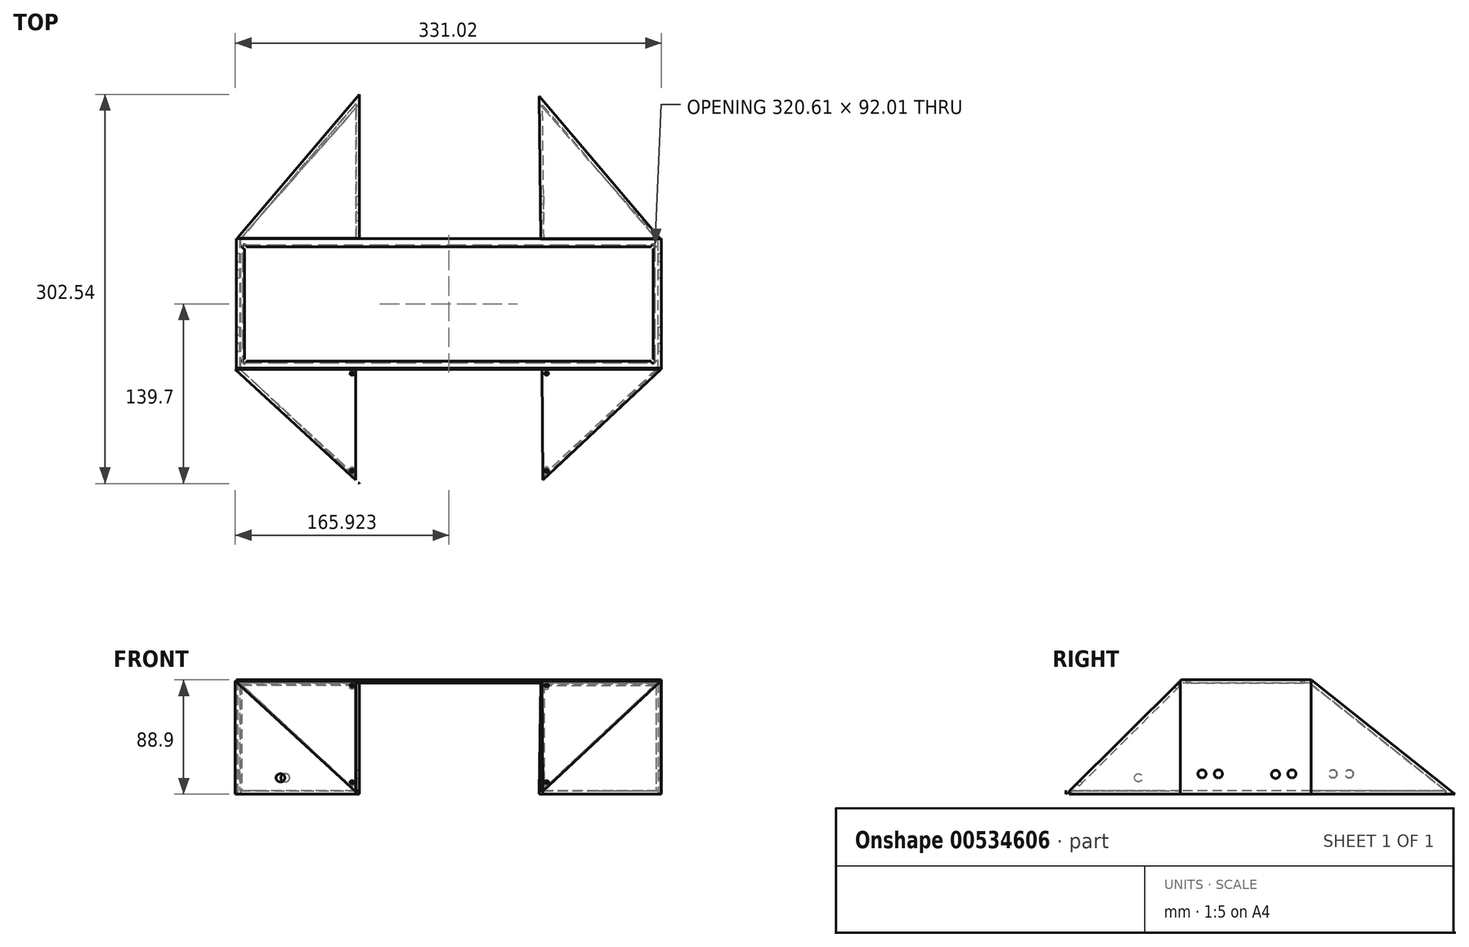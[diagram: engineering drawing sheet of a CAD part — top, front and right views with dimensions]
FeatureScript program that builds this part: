
annotation { "Feature Type Name" : "Feature", "Feature Type Description" : "" }
export const myFeature = defineFeature(function(context is Context, id is Id, definition is map)
    precondition{}
    {
        {
            var Q0;
            Q0=qCreatedBy(makeId("Right.planeOp"),FACE);
            var sketch = newSketch(context, id + "F0", { "sketchPlane" : qUnion([Q0])});
            skLineSegment(sketch, "E0", {"start": v(0, 0) * mm, "end": v(-88.9, 0) * mm});
            skLineSegment(sketch, "E1", {"start": v(-88.9, 0) * mm, "end": v(0, 88.9) * mm});
            skLineSegment(sketch, "E2", {"start": v(101.6, 0) * mm, "end": v(215.9, 0) * mm});
            skLineSegment(sketch, "E3", {"start": v(101.6, 0) * mm, "end": v(101.6, 88.9) * mm});
            skLineSegment(sketch, "E4", {"start": v(0, 88.9) * mm, "end": v(0, 0) * mm});
            skLineSegment(sketch, "E5", {"start": v(101.6, 88.9) * mm, "end": v(215.9, 0) * mm});
            skSolve(sketch);
        }
        {
            var Q0;
            Q0=qCreatedBy(makeId("Top.planeOp"),FACE);
            var sketch = newSketch(context, id + "F1", { "sketchPlane" : qUnion([Q0])});
            skLineSegment(sketch, "E6", {"start": v(-95.65, 101.6) * mm, "end": v(-95.65, 0) * mm});
            skLineSegment(sketch, "E7", {"start": v(234.55, 0) * mm, "end": v(234.55, 101.6) * mm});
            skLineSegment(sketch, "E8", {"start": v(-95.65, 0) * mm, "end": v(234.55, 0) * mm});
            skLineSegment(sketch, "E9", {"start": v(234.55, 101.6) * mm, "end": v(-95.65, 101.6) * mm});
            skSolve(sketch);
        }
        {
            var Q0;
            Q0=makeQuery(id+"F1.imprint","IMPRINT",FACE,{"disambiguationData":[TD([[makeQuery(id+"F1.imprint","IMPRINT",EDGE,{"derivedFrom":sQuery(id+"F1.wireOp",EDGE,"E6")}),1.0]])]});
            extrude(context, id + "F2", {"entities" : qUnion([Q0]), "depth" : 88.9 * mm, "offsetDistance" : 25.4 * mm});
        }
        {
            var Q0;
            Q0=makeQuery(id+"F2.opExtrude","SWEPT_FACE",FACE,{"disambiguationData":[OSD([sQuery(id+"F1.wireOp",EDGE,"E8")])]});
            var Q1;
            Q1=makeQuery(id+"F2.opExtrude","SWEPT_FACE",FACE,{"disambiguationData":[OSD([sQuery(id+"F1.wireOp",EDGE,"E9")])]});
            shell(context, id + "F3", {"entities" : qUnion([Q0, Q1]), "thickness" : 2.54 * mm});
        }
        {
            var Q0;
            Q0=qCreatedBy(makeId("Top.planeOp"),FACE);
            var sketch = newSketch(context, id + "F4", { "sketchPlane" : qUnion([Q0])});
            skLineSegment(sketch, "E10", {"start": v(0, 213.64) * mm, "end": v(-94.8, 102.22) * mm});
            skLineSegment(sketch, "E11", {"start": v(0, 213.64) * mm, "end": v(0, 101.72) * mm});
            skLineSegment(sketch, "E12", {"start": v(0, 101.72) * mm, "end": v(-94.8, 102.22) * mm});
            skLineSegment(sketch, "E13", {"start": v(139.7, 212.38) * mm, "end": v(233.9, 101.28) * mm});
            skLineSegment(sketch, "E14", {"start": v(233.9, 101.28) * mm, "end": v(140.82, 101.28) * mm});
            skLineSegment(sketch, "E15", {"start": v(140.82, 101.28) * mm, "end": v(139.7, 212.38) * mm});
            skLineSegment(sketch, "E16", {"start": v(0, -88.9) * mm, "end": v(-96.47, 0) * mm});
            skLineSegment(sketch, "E17", {"start": v(-96.47, 0) * mm, "end": v(0, 0) * mm});
            skLineSegment(sketch, "E18", {"start": v(0, 0) * mm, "end": v(0, -88.9) * mm});
            skLineSegment(sketch, "E19", {"start": v(234.3, 0) * mm, "end": v(139.7, -88.9) * mm});
            skLineSegment(sketch, "E20", {"start": v(139.7, -88.9) * mm, "end": v(138.93, 0) * mm});
            skLineSegment(sketch, "E21", {"start": v(138.93, 0) * mm, "end": v(234.3, 0) * mm});
            skSolve(sketch);
        }
        {
            var Q0;
            Q0 = qSketchRegion(id + "F4", true);
            extrude(context, id + "F5", {"entities" : qUnion([Q0]), "depth" : 88.9 * mm, "offsetDistance" : 25.4 * mm});
        }
        {
            var Q0;
            Q0=qCreatedBy(makeId("Right.planeOp"),FACE);
            var sketch = newSketch(context, id + "F6", { "sketchPlane" : qUnion([Q0])});
            skLineSegment(sketch, "E22", {"start": v(55.29, 143) * mm, "end": v(-109.68, 111.35) * mm});
            skLineSegment(sketch, "E23", {"start": v(-109.68, 111.35) * mm, "end": v(-88.32, 0) * mm});
            skLineSegment(sketch, "E24", {"start": v(-88.32, 0) * mm, "end": v(55.29, 143) * mm});
            skLineSegment(sketch, "E25", {"start": v(101.57, 88.88) * mm, "end": v(213.71, 0) * mm});
            skLineSegment(sketch, "E26", {"start": v(101.57, 88.88) * mm, "end": v(221.04, 116.12) * mm});
            skLineSegment(sketch, "E27", {"start": v(221.04, 116.12) * mm, "end": v(213.71, 0) * mm});
            skSolve(sketch);
        }
        {
            var Q0;
            Q0 = qSketchRegion(id + "F6", true);
            extrude(context, id + "F7", {"entities" : qUnion([Q0]), "operationType" : NewBodyOperationType.REMOVE, "oppositeDirection" : true, "depth" : 254 * mm, "offsetDistance" : 25.4 * mm});
        }
        {
            var Q0;
            Q0 = qSketchRegion(id + "F6", true);
            extrude(context, id + "F8", {"entities" : qUnion([Q0]), "operationType" : NewBodyOperationType.REMOVE, "depth" : 381 * mm, "offsetDistance" : 25.4 * mm});
        }
        {
            var Q0;
            Q0=qCreatedBy(makeId("Top.planeOp"),FACE);
            var sketch = newSketch(context, id + "F9", { "sketchPlane" : qUnion([Q0])});
            skLineSegment(sketch, "E28.bottom", {"start": v(-89.3, 95.25) * mm, "end": v(228.2, 95.25) * mm});
            skLineSegment(sketch, "E28.top", {"start": v(-89.3, 6.35) * mm, "end": v(228.2, 6.35) * mm});
            skLineSegment(sketch, "E28.left", {"start": v(-89.3, 95.25) * mm, "end": v(-89.3, 6.35) * mm});
            skLineSegment(sketch, "E28.right", {"start": v(228.2, 95.25) * mm, "end": v(228.2, 6.35) * mm});
            skSolve(sketch);
        }
        {
            var Q0;
            Q0 = qSketchRegion(id + "F9", true);
            var Q1;
            Q1=makeQuery(id+"F2.opExtrude","CAP_FACE",FACE,{"disambiguationData":[OSD([sQuery(id+"F1.wireOp",EDGE,"E6"),sQuery(id+"F1.wireOp",EDGE,"E7"),sQuery(id+"F1.wireOp",EDGE,"E8"),sQuery(id+"F1.wireOp",EDGE,"E9")])],"isStart":false});
            extrude(context, id + "F10", {"entities" : qUnion([Q0]), "operationType" : NewBodyOperationType.REMOVE, "depth" : 139.7 * mm, "endBoundEntityFace" : qUnion([Q1]), "hasOffset" : true, "offsetDistance" : 50.8 * mm, "offsetOppositeDirection" : true, "hasSecondDirection" : true, "secondDirectionOppositeDirection" : false, "secondDirectionDepth" : 47 * mm});
        }
        {
            var Q0;
            Q0=qCreatedBy(makeId("Right.planeOp"),FACE);
            var sketch = newSketch(context, id + "F11", { "sketchPlane" : qUnion([Q0])});
            skPoint(sketch, "E29", {"position": v(-32.35, 12.7) * mm});
            skCircle(sketch, "E30", {"center": v(-32.35, 12.7) * mm, "radius": 3.18 * mm});
            skSolve(sketch);
        }
        {
            var Q0;
            Q0=makeQuery(id+"F5.opExtrude","SWEPT_FACE",FACE,{"disambiguationData":[OSD([sQuery(id+"F4.wireOp",EDGE,"E12")])]});
            var Q1;
            Q1=makeQuery(id+"F5.opExtrude","SWEPT_FACE",FACE,{"disambiguationData":[OSD([sQuery(id+"F4.wireOp",EDGE,"E14")])]});
            var Q2;
            Q2=makeQuery(id+"F5.opExtrude","SWEPT_FACE",FACE,{"disambiguationData":[OSD([sQuery(id+"F4.wireOp",EDGE,"E17")])]});
            var Q3;
            Q3=makeQuery(id+"F5.opExtrude","SWEPT_FACE",FACE,{"disambiguationData":[OSD([sQuery(id+"F4.wireOp",EDGE,"E21")])]});
            shell(context, id + "F12", {"entities" : qUnion([Q0, Q1, Q2, Q3]), "thickness" : 2.54 * mm});
        }
        {
            var Q0;
            Q0=makeQuery(id+"F0.imprint","IMPRINT",FACE,{"disambiguationData":[TD([[makeQuery(id+"F0.imprint","IMPRINT",EDGE,{"derivedFrom":sQuery(id+"F0.wireOp",EDGE,"E0")}),-1.0]])]});
            var Q1;
            Q1=makeQuery(id+"F18.boolean.opBoolean","SPLIT",FACE,{"disambiguationData":[TD([makeQuery(id+"F5.opExtrude","SWEPT_FACE",FACE,{"disambiguationData":[OSD([sQuery(id+"F4.wireOp",EDGE,"E21")])]})])],"derivedFrom":makeQuery(id+"F5.opExtrude","SWEPT_FACE",FACE,{"disambiguationData":[OSD([sQuery(id+"F4.wireOp",EDGE,"E20")])]})});
            extrude(context, id + "F13", {"entities" : qUnion([Q0, Q1]), "operationType" : NewBodyOperationType.REMOVE, "endBound" : BoundingType.SYMMETRIC, "oppositeDirection" : true, "depth" : 5.84 * mm, "offsetDistance" : 25.4 * mm});
        }
        {
            var Q0;
            Q0 = qSketchRegion(id + "F11", true);
            extrude(context, id + "F14", {"entities" : qUnion([Q0]), "operationType" : NewBodyOperationType.REMOVE, "oppositeDirection" : true, "depth" : 127 * mm, "offsetDistance" : 25.4 * mm});
        }
        {
            var Q0;
            Q0=qCreatedBy(makeId("Top.planeOp"),FACE);
            var sketch = newSketch(context, id + "F15", { "sketchPlane" : qUnion([Q0])});
            skLineSegment(sketch, "E31.bottom", {"start": v(-89.3, 76.2) * mm, "end": v(-54.3, 76.2) * mm});
            skLineSegment(sketch, "E31.top", {"start": v(-89.3, 25.4) * mm, "end": v(-54.3, 25.4) * mm});
            skLineSegment(sketch, "E31.left", {"start": v(-89.3, 76.2) * mm, "end": v(-89.3, 25.4) * mm});
            skLineSegment(sketch, "E31.right", {"start": v(-54.3, 76.2) * mm, "end": v(-54.3, 25.4) * mm});
            skLineSegment(sketch, "E32.bottom", {"start": v(193.2, 76.2) * mm, "end": v(228.2, 76.2) * mm});
            skLineSegment(sketch, "E32.top", {"start": v(193.2, 25.4) * mm, "end": v(228.2, 25.4) * mm});
            skLineSegment(sketch, "E32.left", {"start": v(193.2, 76.2) * mm, "end": v(193.2, 25.4) * mm});
            skLineSegment(sketch, "E32.right", {"start": v(228.2, 76.2) * mm, "end": v(228.2, 25.4) * mm});
            skSolve(sketch);
        }
        {
            var Q0;
            Q0 = qSketchRegion(id + "F15", true);
            extrude(context, id + "F16", {"entities" : qUnion([Q0]), "operationType" : NewBodyOperationType.REMOVE, "depth" : 25.4 * mm, "offsetDistance" : 25.4 * mm});
        }
        {
            var Q0;
            Q0=qCreatedBy(makeId("Top.planeOp"),FACE);
            var sketch = newSketch(context, id + "F17", { "sketchPlane" : qUnion([Q0])});
            skLineSegment(sketch, "E33", {"start": v(-92.35, 0) * mm, "end": v(0, -87.18) * mm});
            skLineSegment(sketch, "E34", {"start": v(0, -87.18) * mm, "end": v(139.7, -87.18) * mm});
            skLineSegment(sketch, "E35", {"start": v(139.7, -87.18) * mm, "end": v(232.05, 0) * mm});
            skLineSegment(sketch, "E36", {"start": v(232.05, 0) * mm, "end": v(232.05, 101.6) * mm});
            skLineSegment(sketch, "E37", {"start": v(232.05, 101.6) * mm, "end": v(139.7, 206.42) * mm});
            skLineSegment(sketch, "E38", {"start": v(139.7, 206.42) * mm, "end": v(0, 206.42) * mm});
            skLineSegment(sketch, "E39", {"start": v(0, 206.42) * mm, "end": v(-92.35, 101.6) * mm});
            skLineSegment(sketch, "E40", {"start": v(-92.35, 101.6) * mm, "end": v(-92.35, 0) * mm});
            skSolve(sketch);
        }
        {
            var Q0;
            Q0 = qSketchRegion(id + "F17", true);
            extrude(context, id + "F18", {"entities" : qUnion([Q0]), "operationType" : NewBodyOperationType.REMOVE, "depth" : 2.54 * mm, "offsetDistance" : 25.4 * mm});
        }
        {
            var Q0;
            Q0=qCreatedBy(makeId("Right.planeOp"),FACE);
            var sketch = newSketch(context, id + "F19", { "sketchPlane" : qUnion([Q0])});
            skCircle(sketch, "E41", {"center": v(86.87, 15.75) * mm, "radius": 3.18 * mm});
            skCircle(sketch, "E42", {"center": v(74.17, 15.39) * mm, "radius": 3.18 * mm});
            skCircle(sketch, "E43", {"center": v(17.02, 15.75) * mm, "radius": 3.18 * mm});
            skCircle(sketch, "E44", {"center": v(29.72, 15.75) * mm, "radius": 3.18 * mm});
            skCircle(sketch, "E45", {"center": v(118.67, 15.75) * mm, "radius": 3.18 * mm});
            skCircle(sketch, "E46", {"center": v(131.37, 15.75) * mm, "radius": 3.18 * mm});
            skSolve(sketch);
        }
        {
            var Q0;
            Q0=makeQuery(id+"F19.imprint","IMPRINT",FACE,{"disambiguationData":[TD([[makeQuery(id+"F19.imprint","IMPRINT",EDGE,{"derivedFrom":sQuery(id+"F19.wireOp",EDGE,"E41")}),1.0]])]});
            var Q1;
            Q1=makeQuery(id+"F19.imprint","IMPRINT",FACE,{"disambiguationData":[TD([[makeQuery(id+"F19.imprint","IMPRINT",EDGE,{"derivedFrom":sQuery(id+"F19.wireOp",EDGE,"E42")}),1.0]])]});
            var Q2;
            Q2=makeQuery(id+"F19.imprint","IMPRINT",FACE,{"disambiguationData":[TD([[makeQuery(id+"F19.imprint","IMPRINT",EDGE,{"derivedFrom":sQuery(id+"F19.wireOp",EDGE,"E43")}),1.0]])]});
            var Q3;
            Q3=makeQuery(id+"F19.imprint","IMPRINT",FACE,{"disambiguationData":[TD([[makeQuery(id+"F19.imprint","IMPRINT",EDGE,{"derivedFrom":sQuery(id+"F19.wireOp",EDGE,"E44")}),1.0]])]});
            extrude(context, id + "F20", {"entities" : qUnion([Q0, Q1, Q2, Q3]), "operationType" : NewBodyOperationType.REMOVE, "endBound" : BoundingType.SYMMETRIC, "oppositeDirection" : true, "depth" : 762 * mm, "offsetDistance" : 25.4 * mm});
        }
        {
            var Q0;
            Q0=makeQuery(id+"F19.imprint","IMPRINT",FACE,{"disambiguationData":[TD([[makeQuery(id+"F19.imprint","IMPRINT",EDGE,{"derivedFrom":sQuery(id+"F19.wireOp",EDGE,"E45")}),1.0]])]});
            var Q1;
            Q1=makeQuery(id+"F19.imprint","IMPRINT",FACE,{"disambiguationData":[TD([[makeQuery(id+"F19.imprint","IMPRINT",EDGE,{"derivedFrom":sQuery(id+"F19.wireOp",EDGE,"E46")}),1.0]])]});
            extrude(context, id + "F21", {"entities" : qUnion([Q0, Q1]), "operationType" : NewBodyOperationType.REMOVE, "depth" : 152.4 * mm, "offsetDistance" : 25.4 * mm});
        }
        {
            var Q0;
            Q0=makeQuery(id+"F19.imprint","IMPRINT",FACE,{"disambiguationData":[TD([[makeQuery(id+"F19.imprint","IMPRINT",EDGE,{"derivedFrom":sQuery(id+"F19.wireOp",EDGE,"E45")}),1.0]])]});
            var Q1;
            Q1=makeQuery(id+"F19.imprint","IMPRINT",FACE,{"disambiguationData":[TD([[makeQuery(id+"F19.imprint","IMPRINT",EDGE,{"derivedFrom":sQuery(id+"F19.wireOp",EDGE,"E46")}),1.0]])]});
            extrude(context, id + "F22", {"entities" : qUnion([Q0, Q1]), "operationType" : NewBodyOperationType.REMOVE, "oppositeDirection" : true, "depth" : 25.4 * mm, "offsetDistance" : 25.4 * mm});
        }
        {
            var Q0;
            Q0=makeQuery(id+"F2.opExtrude","CAP_FACE",FACE,{"disambiguationData":[OSD([sQuery(id+"F1.wireOp",EDGE,"E6"),sQuery(id+"F1.wireOp",EDGE,"E7"),sQuery(id+"F1.wireOp",EDGE,"E8"),sQuery(id+"F1.wireOp",EDGE,"E9")])],"isStart":false});
            var sketch = newSketch(context, id + "F23", { "sketchPlane" : qUnion([Q0])});
            skPoint(sketch, "E47", {"position": v(-89.3, 95.25) * mm});
            skPoint(sketch, "E48", {"position": v(-89.3, 6.35) * mm});
            skPoint(sketch, "E49", {"position": v(228.2, 6.35) * mm});
            skPoint(sketch, "E50", {"position": v(228.2, 95.25) * mm});
            skSolve(sketch);
        }
        {
            var Q0;
            Q0=sQuery(id+"F23.wireOp",VERTEX,"E47");
            var Q1;
            Q1=sQuery(id+"F23.wireOp",VERTEX,"E48");
            var Q2;
            Q2=sQuery(id+"F23.wireOp",VERTEX,"E49");
            var Q3;
            Q3=sQuery(id+"F23.wireOp",VERTEX,"E50");
            var Q4;
            Q4=makeQuery(id+"F2.opExtrude","SWEPT_BODY",BODY,{"disambiguationData":[OSD([sQuery(id+"F1.wireOp",EDGE,"E6"),sQuery(id+"F1.wireOp",EDGE,"E7"),sQuery(id+"F1.wireOp",EDGE,"E8"),sQuery(id+"F1.wireOp",EDGE,"E9")])]});
            var Q5;
            Q5=makeQuery(id+"F5.opExtrude","SWEPT_BODY",BODY,{"disambiguationData":[OSD([sQuery(id+"F4.wireOp",EDGE,"E10"),sQuery(id+"F4.wireOp",EDGE,"E11"),sQuery(id+"F4.wireOp",EDGE,"E12")])]});
            var Q6;
            Q6=makeQuery(id+"F5.opExtrude","SWEPT_BODY",BODY,{"disambiguationData":[OSD([sQuery(id+"F4.wireOp",EDGE,"E13"),sQuery(id+"F4.wireOp",EDGE,"E14"),sQuery(id+"F4.wireOp",EDGE,"E15")])]});
            var Q7;
            Q7=makeQuery(id+"F7.boolean.opBoolean","SPLIT",BODY,{"disambiguationData":[OD(0.0)],"derivedFrom":makeQuery(id+"F5.opExtrude","SWEPT_BODY",BODY,{"disambiguationData":[OSD([sQuery(id+"F4.wireOp",EDGE,"E16"),sQuery(id+"F4.wireOp",EDGE,"E17"),sQuery(id+"F4.wireOp",EDGE,"E18")])]})});
            var Q8;
            Q8=makeQuery(id+"F7.boolean.opBoolean","SPLIT",BODY,{"disambiguationData":[OD(1.0)],"derivedFrom":makeQuery(id+"F5.opExtrude","SWEPT_BODY",BODY,{"disambiguationData":[OSD([sQuery(id+"F4.wireOp",EDGE,"E16"),sQuery(id+"F4.wireOp",EDGE,"E17"),sQuery(id+"F4.wireOp",EDGE,"E18")])]})});
            var Q9;
            Q9=makeQuery(id+"F8.boolean.opBoolean","SPLIT",BODY,{"disambiguationData":[OD(1.0)],"derivedFrom":makeQuery(id+"F5.opExtrude","SWEPT_BODY",BODY,{"disambiguationData":[OSD([sQuery(id+"F4.wireOp",EDGE,"E19"),sQuery(id+"F4.wireOp",EDGE,"E20"),sQuery(id+"F4.wireOp",EDGE,"E21")])]})});
            hole(context, id + "F24", {"style" : HoleStyle.SIMPLE, "endStyle" : HoleEndStyle.BLIND, "holeDiameter" : 3.17 * mm, "holeDepth" : 254 * mm, "isTappedThrough" : true, "tappedDepth" : 12.7 * mm, "tapClearance" : 3, "locations" : qUnion([Q0, Q1, Q2, Q3]), "scope" : qUnion([Q4, Q5, Q6, Q7, Q8, Q9])});
        }
        {
            var Q0;
            {var subQ0=sQuery(id+"F4.wireOp",EDGE,"E16");Q0=makeQuery(id+"F7.boolean.opBoolean","COPY",FACE,{"disambiguationData":[TD([makeQuery(id+"F5.opExtrude","SWEPT_FACE",FACE,{"disambiguationData":[OSD([subQ0])]})])],"derivedFrom":makeQuery(id+"F7.opExtrude","SWEPT_FACE",FACE,{"disambiguationData":[OSD([sQuery(id+"F6.wireOp",EDGE,"E24")])]})});}
            var sketch = newSketch(context, id + "F25", { "sketchPlane" : qUnion([Q0])});
            skPoint(sketch, "E51", {"position": v(-5.69, 57.17) * mm});
            skPoint(sketch, "E52", {"position": v(145.42, 57.17) * mm});
            skPoint(sketch, "E53", {"position": v(-5.69, -49.41) * mm});
            skPoint(sketch, "E54", {"position": v(145.42, -49.41) * mm});
            skSolve(sketch);
        }
        {
            var Q0;
            Q0=sQuery(id+"F25.wireOp",VERTEX,"E51");
            var Q1;
            Q1=sQuery(id+"F25.wireOp",VERTEX,"E53");
            var Q2;
            Q2=sQuery(id+"F25.wireOp",VERTEX,"E52");
            var Q3;
            Q3=sQuery(id+"F25.wireOp",VERTEX,"E54");
            var Q4;
            Q4=makeQuery(id+"F7.boolean.opBoolean","SPLIT",BODY,{"disambiguationData":[OD(1.0)],"derivedFrom":makeQuery(id+"F5.opExtrude","SWEPT_BODY",BODY,{"disambiguationData":[OSD([sQuery(id+"F4.wireOp",EDGE,"E16"),sQuery(id+"F4.wireOp",EDGE,"E17"),sQuery(id+"F4.wireOp",EDGE,"E18")])]})});
            var Q5;
            Q5=makeQuery(id+"F8.boolean.opBoolean","SPLIT",BODY,{"disambiguationData":[OD(1.0)],"derivedFrom":makeQuery(id+"F5.opExtrude","SWEPT_BODY",BODY,{"disambiguationData":[OSD([sQuery(id+"F4.wireOp",EDGE,"E19"),sQuery(id+"F4.wireOp",EDGE,"E20"),sQuery(id+"F4.wireOp",EDGE,"E21")])]})});
            hole(context, id + "F26", {"style" : HoleStyle.SIMPLE, "endStyle" : HoleEndStyle.BLIND, "holeDiameter" : 3.17 * mm, "holeDepth" : 254 * mm, "isTappedThrough" : true, "tappedDepth" : 12.7 * mm, "tapClearance" : 3, "locations" : qUnion([Q0, Q1, Q2, Q3]), "scope" : qUnion([Q4, Q5])});
        }
    });
